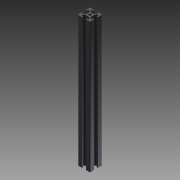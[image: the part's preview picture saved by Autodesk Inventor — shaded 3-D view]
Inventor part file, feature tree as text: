
AUTODESK INVENTOR PART (.ipt)
format: ipt  version: 2014 SP1 (Build 180222100, 222)  size: 172,032 bytes
history: native  units: mm
features: other x7, sketch x2, extrude x1, revolve x1
ambient origin geometry x8: Origin, YZ Plane, XZ Plane, XY Plane, X Axis, Y Axis, Z Axis, Center Point
bodies: Solid1 (feature_tree)
feature tree (11):
  extrude  "Extrusion1"  TaperAngle=360.0deg  [1 undecoded]
  revolve  "Revolution1"  [1 undecoded]
  other  "C1_XY"
  other  "C1_YZ"
  other  "C1_ZX"
  other  "C1_X"
  other  "C1_Y"
  other  "C1_Z"
  other  "C1_Center"
  sketch  "Sketch_1"  dims[d0=214.0mm d1=0.0mm d2=360.0deg]
  sketch  "Sketch_2"
note: 2 required parameter values undecoded (feature->parameter linkage not recoverable at this tier; creation-order binding heuristic only, values carry confidence <= 0.55)
